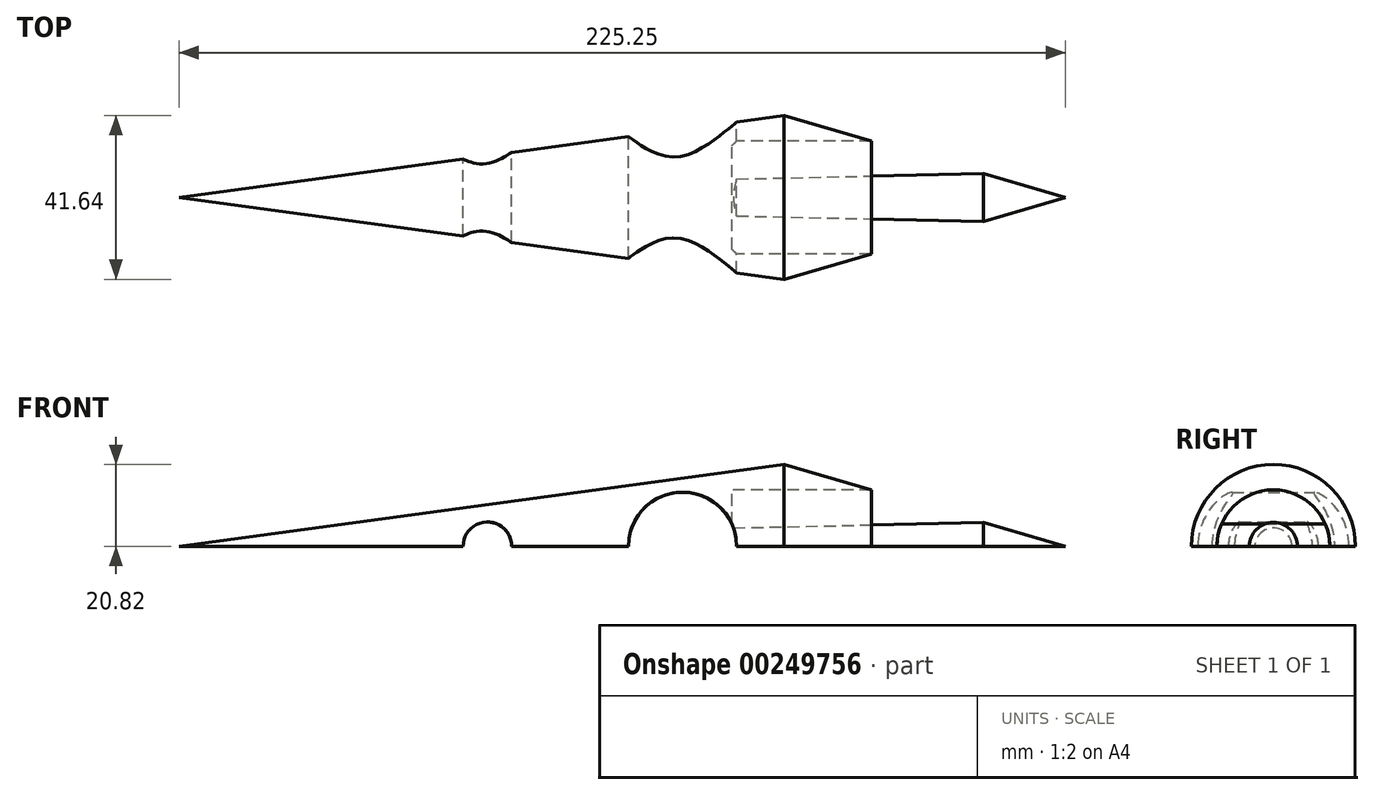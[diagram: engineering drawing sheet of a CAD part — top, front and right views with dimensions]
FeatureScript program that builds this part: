
annotation { "Feature Type Name" : "Feature", "Feature Type Description" : "" }
export const myFeature = defineFeature(function(context is Context, id is Id, definition is map)
    precondition{}
    {
        {
            var Q0;
            Q0=qCreatedBy(makeId("Top.planeOp"),FACE);
            var sketch = newSketch(context, id + "F0", { "sketchPlane" : qUnion([Q0])});
            skLineSegment(sketch, "E0", {"start": v(0, 0) * mm, "end": v(153.72, 20.82) * mm});
            skLineSegment(sketch, "E1", {"start": v(0, 0) * mm, "end": v(225.25, 0) * mm});
            skLineSegment(sketch, "E2", {"start": v(225.25, 0) * mm, "end": v(204.4, 6.07) * mm});
            skLineSegment(sketch, "E3", {"start": v(175.97, 14.34) * mm, "end": v(140.47, 14.34) * mm});
            skLineSegment(sketch, "E4", {"start": v(140.47, 14.34) * mm, "end": v(140.47, 4.67) * mm});
            skLineSegment(sketch, "E5", {"start": v(140.47, 4.67) * mm, "end": v(204.4, 6.07) * mm});
            skLineSegment(sketch, "E6.trimOffspring", {"start": v(175.97, 14.34) * mm, "end": v(153.72, 20.82) * mm});
            skSolve(sketch);
        }
        {
            var Q0;
            Q0=makeQuery(id+"F0.imprint","IMPRINT",FACE,{"disambiguationData":[TD([[makeQuery(id+"F0.imprint","IMPRINT",EDGE,{"derivedFrom":sQuery(id+"F0.wireOp",EDGE,"E0")}),-1.0]])]});
            var Q1;
            Q1=sQuery(id+"F0.wireOp",EDGE,"E1");
            var Q2;
            Q2=sQuery(id+"F0.wireOp",EDGE,"E0");
            var Q3;
            Q3=sQuery(id+"F0.wireOp",EDGE,"E6.trimOffspring");
            var Q4;
            Q4=sQuery(id+"F0.wireOp",EDGE,"E3");
            var Q5;
            Q5=sQuery(id+"F0.wireOp",EDGE,"E1");
            revolve(context, id + "F1", {"entities" : qUnion([Q0]), "surfaceEntities" : qUnion([Q1, Q2, Q3, Q4]), "axis" : qUnion([Q5]), "revolveType" : RevolveType.ONE_DIRECTION, "angle" : 180 * degree});
        }
        {
            var Q0;
            Q0=qCreatedBy(makeId("Front.planeOp"),FACE);
            var sketch = newSketch(context, id + "F2", { "sketchPlane" : qUnion([Q0])});
            skCircle(sketch, "E7", {"center": v(78.4, 0) * mm, "radius": 6.18 * mm});
            skCircle(sketch, "E8", {"center": v(127.95, 0) * mm, "radius": 13.76 * mm});
            skSolve(sketch);
        }
        {
            var Q0;
            Q0 = qSketchRegion(id + "F2", true);
            extrude(context, id + "F3", {"entities" : qUnion([Q0]), "operationType" : NewBodyOperationType.REMOVE, "endBound" : BoundingType.SYMMETRIC, "depth" : 50.8 * mm});
        }
    });
